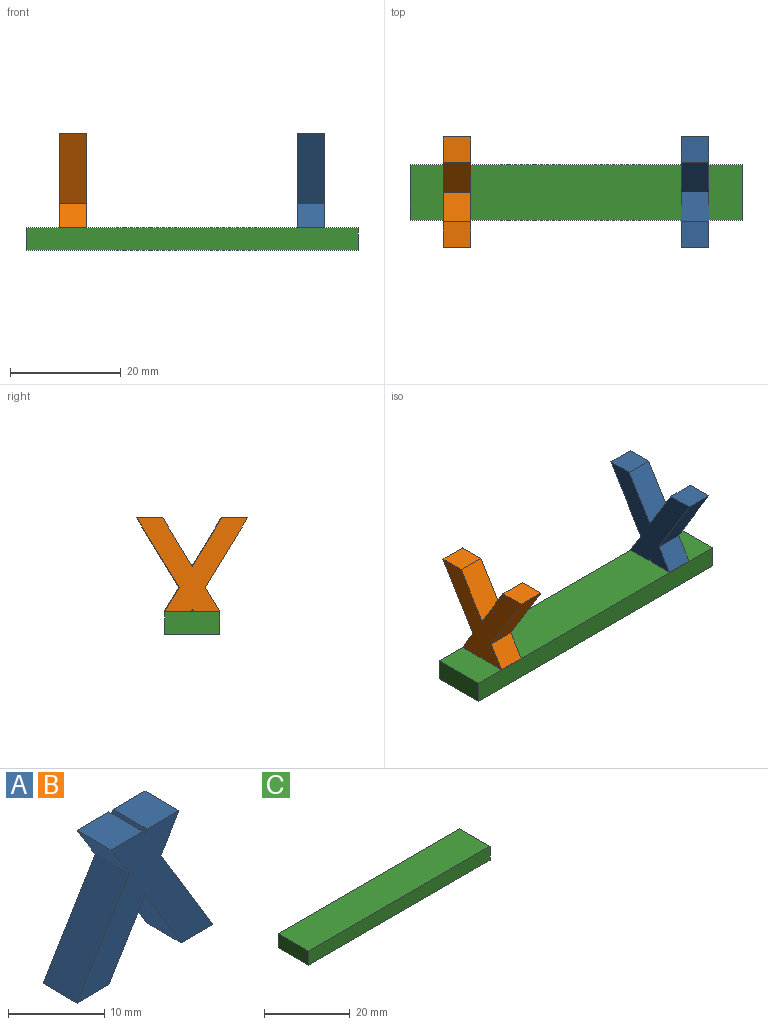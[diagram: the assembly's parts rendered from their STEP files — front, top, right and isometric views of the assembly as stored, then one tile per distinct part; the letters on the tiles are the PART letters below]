
ASSEMBLY  parts=3 mates=4
PART A: 14 faces, bbox 20x5x17 mm
  f0: plane 5x0.53mm, normal (0.85,0,0.52), area 3.1mm2, adj f1,f11,f12,f13
  f1: plane 5x4.68mm, normal (0,0,1), area 23.4mm2, adj f0,f2,f12,f13
  f2: plane 5x4.38mm, normal (-0.85,0,-0.52), area 25.6mm2, adj f1,f3,f12,f13
  f3: plane 12.62x7.66mm, normal (-0.85,0,0.52), area 73.8mm2, adj f2,f4,f12,f13
  f4: plane 5x4.68mm, normal (0,0,-1), area 23.4mm2, adj f3,f5,f12,f13
  f5: plane 8.76x5.32mm, normal (0.85,0,-0.52), area 51.3mm2, adj f4,f6,f12,f13
  f6: plane 8.76x5.32mm, normal (-0.85,0,-0.52), area 51.3mm2, adj f5,f7,f12,f13
  f7: plane 5x4.68mm, normal (0,0,-1), area 23.4mm2, adj f6,f8,f12,f13
  f8: plane 12.62x7.66mm, normal (0.85,0,0.52), area 73.8mm2, adj f7,f9,f12,f13
  f9: plane 5x4.38mm, normal (0.85,0,-0.52), area 25.6mm2, adj f8,f10,f12,f13
  f10: plane 5x4.68mm, normal (0,0,1), area 23.4mm2, adj f9,f11,f12,f13
  f11: plane 5x0.53mm, normal (-0.85,0,0.52), area 3.1mm2, adj f0,f10,f12,f13
  f12: plane 20x17mm, normal (0,-1,0), area 141.1mm2, adj f0,f1,f2,f3,f4,f5,f6,f7
  f13: plane 20x17mm, normal (0,1,0), area 141.1mm2, adj f0,f1,f2,f3,f4,f5,f6,f7
PART B: same geometry as A
PART C: 6 faces, bbox 60x10x4 mm
  f0: plane 60x4mm, normal (0,-1,0), area 240mm2, adj f1,f3,f4,f5
  f1: plane 10x4mm, normal (1,0,0), area 40mm2, adj f0,f2,f4,f5
  f2: plane 60x4mm, normal (0,1,0), area 240mm2, adj f1,f3,f4,f5
  f3: plane 10x4mm, normal (-1,0,0), area 40mm2, adj f0,f2,f4,f5
  f4: plane 60x10mm, normal (0,0,1), area 600mm2, adj f0,f1,f2,f3
  f5: plane 60x10mm, normal (0,0,-1), area 600mm2, adj f0,f1,f2,f3
PLACE A rot(axis=(-0.71,-0.71,0),180deg) t=(40.75,-2.8,-12.84)mm
PLACE B rot(axis=(-0.71,-0.71,0),180deg) t=(-2.25,-2.89,-12.84)mm
PLACE C rot(axis=(-1,0,0),180deg) t=(46.75,2.11,-12.84)mm
MATE planar C.f5 <-> B.f10  axis (0,0,1) through (16.75,-2.89,-12.84)mm
MATE parallel B.f12 <-> C.f3  axis (-1,0,0) through (-7.25,-2.89,-12.31)mm
MATE planar A.f10 <-> C.f5  axis (0,0,-1) through (38.25,-0.14,-12.84)mm
MATE parallel A.f13 <-> C.f1  axis (1,0,0) through (40.75,-2.8,-12.31)mm
